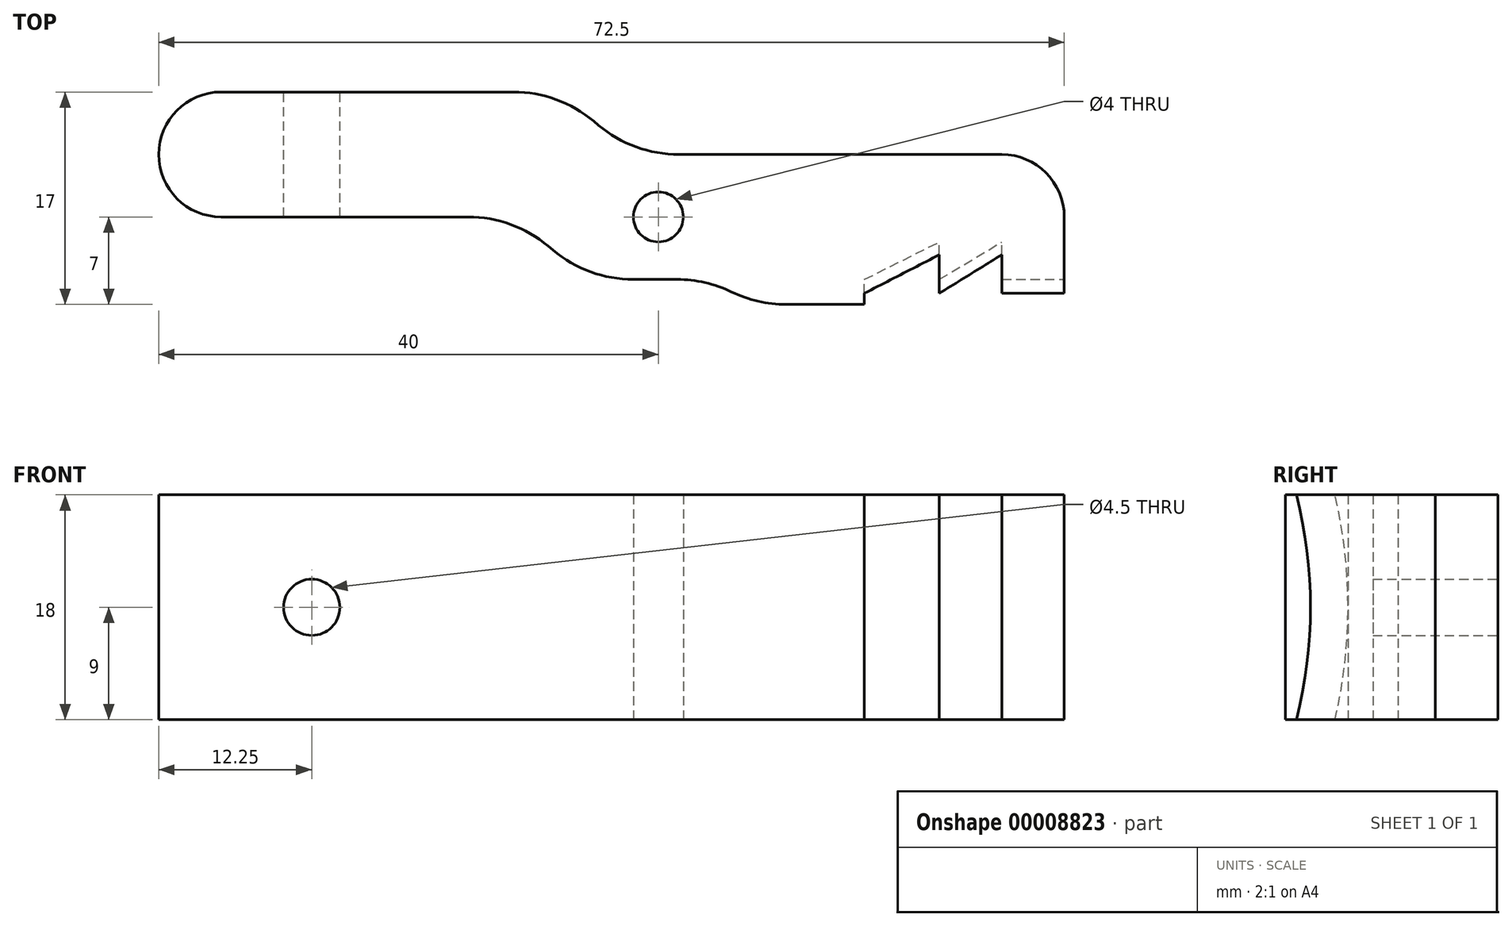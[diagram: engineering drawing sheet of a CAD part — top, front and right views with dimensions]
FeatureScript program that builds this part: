
annotation { "Feature Type Name" : "Feature", "Feature Type Description" : "" }
export const myFeature = defineFeature(function(context is Context, id is Id, definition is map)
    precondition{}
    {
        {
            var Q0;
            Q0=qCreatedBy(makeId("Top.planeOp"),FACE);
            var sketch = newSketch(context, id + "F0", { "sketchPlane" : qUnion([Q0])});
            skCircle(sketch, "E0", {"center": v(0, 0) * mm, "radius": 2 * mm});
            skLineSegment(sketch, "E1", {"start": v(0, -5) * mm, "end": v(7.5, -5) * mm});
            skLineSegment(sketch, "E2", {"start": v(7.5, -5) * mm, "end": v(7.5, -7) * mm});
            skLineSegment(sketch, "E3", {"start": v(7.5, -7) * mm, "end": v(32.5, -7) * mm});
            skLineSegment(sketch, "E4", {"start": v(32.5, -7) * mm, "end": v(32.5, 5) * mm});
            skLineSegment(sketch, "E5", {"start": v(32.5, 5) * mm, "end": v(0, 5) * mm});
            skLineSegment(sketch, "E6", {"start": v(0, 5) * mm, "end": v(0, -5) * mm, "construction": true});
            skLineSegment(sketch, "E7", {"start": v(0, 5) * mm, "end": v(-2, 5) * mm});
            skLineSegment(sketch, "E8", {"start": v(-2, 5) * mm, "end": v(-7.96, 10) * mm});
            skLineSegment(sketch, "E9", {"start": v(-7.96, 10) * mm, "end": v(-40, 10) * mm});
            skLineSegment(sketch, "E10", {"start": v(-40, 10) * mm, "end": v(-40, 0) * mm});
            skLineSegment(sketch, "E11", {"start": v(-40, 0) * mm, "end": v(-11.6, 0) * mm});
            skLineSegment(sketch, "E12", {"start": v(-11.6, 0) * mm, "end": v(-5.64, -5) * mm});
            skLineSegment(sketch, "E13", {"start": v(-5.64, -5) * mm, "end": v(0, -5) * mm});
            skPoint(sketch, "E14", {"position": v(-2, 0) * mm});
            skSolve(sketch);
        }
        {
            var Q0;
            Q0=makeQuery(id+"F0.imprint","IMPRINT",FACE,{"disambiguationData":[TD([[makeQuery(id+"F0.imprint","IMPRINT",EDGE,{"derivedFrom":sQuery(id+"F0.wireOp",EDGE,"E0")}),-1.0]])]});
            extrude(context, id + "F1", {"entities" : qUnion([Q0]), "endBound" : BoundingType.SYMMETRIC, "depth" : 18 * mm});
        }
        {
            var Q0;
            Q0=qCreatedBy(makeId("Top.planeOp"),FACE);
            var sketch = newSketch(context, id + "F2", { "sketchPlane" : qUnion([Q0])});
            skLineSegment(sketch, "E15.0.0", {"start": v(-50, 5) * mm, "end": v(-50, -5) * mm});
            skLineSegment(sketch, "E15.0.1", {"start": v(-50, -5) * mm, "end": v(7.5, -5) * mm});
            skLineSegment(sketch, "E15.0.2", {"start": v(7.5, -5) * mm, "end": v(7.5, -7) * mm});
            skLineSegment(sketch, "E15.0.3", {"start": v(7.5, -7) * mm, "end": v(32.5, -7) * mm});
            skLineSegment(sketch, "E15.0.4", {"start": v(32.5, -7) * mm, "end": v(32.5, 5) * mm});
            skLineSegment(sketch, "E15.0.5", {"start": v(32.5, 5) * mm, "end": v(-50, 5) * mm});
            skLineSegment(sketch, "E16", {"start": v(32.5, -5) * mm, "end": v(27.5, -5) * mm});
            skLineSegment(sketch, "E17", {"start": v(27.5, -5) * mm, "end": v(27.5, -2) * mm});
            skLineSegment(sketch, "E18", {"start": v(27.5, -2) * mm, "end": v(22.5, -5) * mm});
            skLineSegment(sketch, "E19", {"start": v(22.5, -5) * mm, "end": v(22.5, -2) * mm});
            skLineSegment(sketch, "E20", {"start": v(22.5, -2) * mm, "end": v(16.5, -5) * mm});
            skLineSegment(sketch, "E21", {"start": v(16.5, -5) * mm, "end": v(16.5, -7) * mm});
            skSolve(sketch);
        }
        {
            var Q0;
            Q0=qCreatedBy(makeId("Right.planeOp"),FACE);
            var sketch = newSketch(context, id + "F3", { "sketchPlane" : qUnion([Q0])});
            skCircle(sketch, "E22", {"center": v(-42, 0) * mm, "radius": 40 * mm});
            skSolve(sketch);
        }
        {
            var Q0;
            {var subQ1=sQuery(id+"F2.wireOp",EDGE,"E16");Q0=makeQuery(id+"F2.imprint","IMPRINT",FACE,{"disambiguationData":[TD([[makeQuery(id+"F2.imprint","IMPRINT",EDGE,{"derivedFrom":subQ1}),1.0]])]});}
            var Q1;
            Q1=sQuery(id+"F3.wireOp",EDGE,"E22");
            sweep(context, id + "F4", {"operationType" : NewBodyOperationType.REMOVE, "profiles" : qUnion([Q0]), "path" : qUnion([Q1])});
        }
        {
            var Q0;
            Q0=makeQuery(id+"F1.opExtrude","SWEPT_EDGE",EDGE,{"disambiguationData":[OSD([sQuery(id+"F0.wireOp",EDGE,"E1"),sQuery(id+"F0.wireOp",EDGE,"E2")])]});
            fillet(context, id + "F5", {"entities" : qUnion([Q0]), "radius" : 10 * mm, "tangentPropagation" : true, "allowEdgeOverflow" : false});
        }
        {
            var Q0;
            Q0=makeQuery(id+"F5.opFillet","BLEND_EDGE",EDGE,{"blendedFrom":[makeQuery(id+"F1.opExtrude","SWEPT_EDGE",EDGE,{"disambiguationData":[OSD([sQuery(id+"F0.wireOp",EDGE,"E1"),sQuery(id+"F0.wireOp",EDGE,"E2")])]}),makeQuery(id+"F1.opExtrude","SWEPT_FACE",FACE,{"disambiguationData":[OSD([sQuery(id+"F0.wireOp",EDGE,"E3")])]})],"blendedInto":[makeQuery(id+"F1.opExtrude","SWEPT_FACE",FACE,{"disambiguationData":[OSD([sQuery(id+"F0.wireOp",EDGE,"E3")])]})]});
            fillet(context, id + "F6", {"entities" : qUnion([Q0]), "radius" : 10 * mm, "tangentPropagation" : true, "allowEdgeOverflow" : false});
        }
        {
            var Q0;
            Q0=makeQuery(id+"F1.opExtrude","SWEPT_EDGE",EDGE,{"disambiguationData":[OSD([sQuery(id+"F0.wireOp",EDGE,"E1"),sQuery(id+"F0.wireOp",EDGE,"c4e45db2-ec65-447f-bea5-91706df0527c")])]});
            var Q1;
            Q1=makeQuery(id+"F1.opExtrude","SWEPT_EDGE",EDGE,{"disambiguationData":[OSD([sQuery(id+"F0.wireOp",EDGE,"E5"),sQuery(id+"F0.wireOp",EDGE,"c4e45db2-ec65-447f-bea5-91706df0527c")])]});
            var Q2;
            Q2=makeQuery(id+"F1.opExtrude","SWEPT_EDGE",EDGE,{"disambiguationData":[OSD([sQuery(id+"F0.wireOp",EDGE,"E4"),sQuery(id+"F0.wireOp",EDGE,"E5")])]});
            fillet(context, id + "F7", {"entities" : qUnion([Q0, Q1, Q2]), "radius" : 5 * mm, "tangentPropagation" : true, "allowEdgeOverflow" : false});
        }
        {
            var Q0;
            Q0=makeQuery(id+"F1.opExtrude","SWEPT_EDGE",EDGE,{"disambiguationData":[OSD([sQuery(id+"F0.wireOp",EDGE,"E12"),sQuery(id+"F0.wireOp",EDGE,"E13")])]});
            var Q1;
            Q1=makeQuery(id+"F1.opExtrude","SWEPT_EDGE",EDGE,{"disambiguationData":[OSD([sQuery(id+"F0.wireOp",EDGE,"E7"),sQuery(id+"F0.wireOp",EDGE,"E8")])]});
            var Q2;
            Q2=makeQuery(id+"F1.opExtrude","SWEPT_EDGE",EDGE,{"disambiguationData":[OSD([sQuery(id+"F0.wireOp",EDGE,"E8"),sQuery(id+"F0.wireOp",EDGE,"E9")])]});
            var Q3;
            Q3=makeQuery(id+"F1.opExtrude","SWEPT_EDGE",EDGE,{"disambiguationData":[OSD([sQuery(id+"F0.wireOp",EDGE,"E11"),sQuery(id+"F0.wireOp",EDGE,"E12")])]});
            fillet(context, id + "F8", {"entities" : qUnion([Q0, Q1, Q2, Q3]), "radius" : 10 * mm, "tangentPropagation" : true, "allowEdgeOverflow" : false});
        }
        {
            var Q0;
            Q0=makeQuery(id+"F1.opExtrude","SWEPT_EDGE",EDGE,{"disambiguationData":[OSD([sQuery(id+"F0.wireOp",EDGE,"E10"),sQuery(id+"F0.wireOp",EDGE,"E11")])]});
            var Q1;
            Q1=makeQuery(id+"F1.opExtrude","SWEPT_EDGE",EDGE,{"disambiguationData":[OSD([sQuery(id+"F0.wireOp",EDGE,"E9"),sQuery(id+"F0.wireOp",EDGE,"E10")])]});
            fillet(context, id + "F9", {"entities" : qUnion([Q0, Q1]), "radius" : 5 * mm, "tangentPropagation" : true, "allowEdgeOverflow" : false});
        }
        {
            var Q0;
            Q0=makeQuery(id+"F1.opExtrude","SWEPT_FACE",FACE,{"disambiguationData":[OSD([sQuery(id+"F0.wireOp",EDGE,"E9")])]});
            var sketch = newSketch(context, id + "F10", { "sketchPlane" : qUnion([Q0])});
            skCircle(sketch, "E23", {"center": v(27.75, 0) * mm, "radius": 2.25 * mm});
            skSolve(sketch);
        }
        {
            var Q0;
            Q0=makeQuery(id+"F10.imprint","IMPRINT",FACE,{"disambiguationData":[TD([[makeQuery(id+"F10.imprint","IMPRINT",EDGE,{"derivedFrom":sQuery(id+"F10.wireOp",EDGE,"E23")}),1.0]])]});
            extrude(context, id + "F11", {"entities" : qUnion([Q0]), "operationType" : NewBodyOperationType.REMOVE, "endBound" : BoundingType.UP_TO_NEXT, "oppositeDirection" : true, "depth" : 25 * mm});
        }
    });
